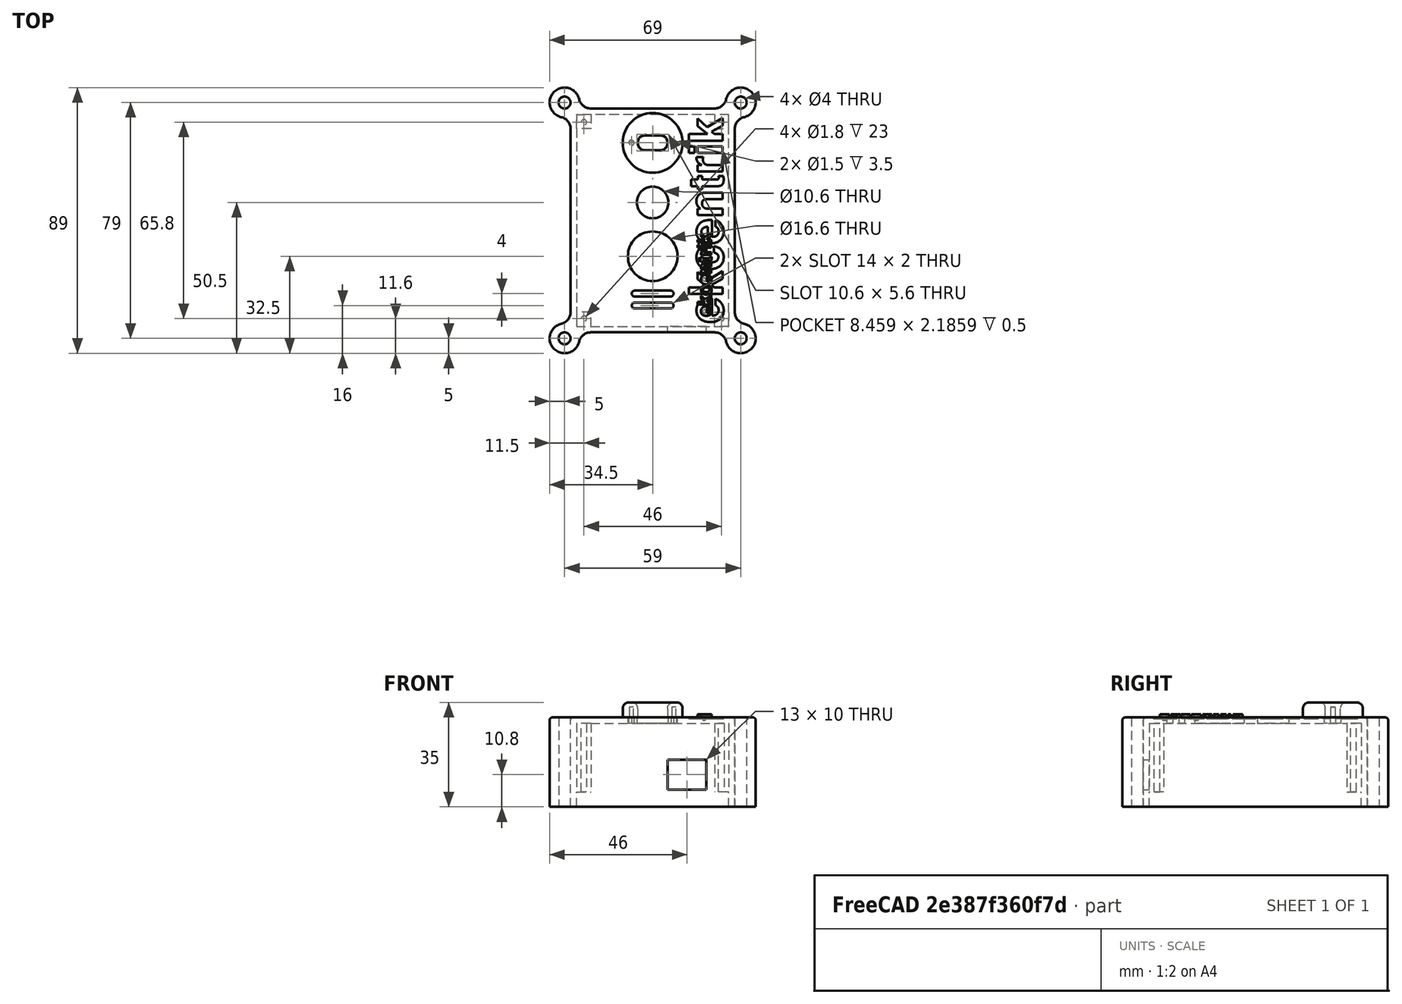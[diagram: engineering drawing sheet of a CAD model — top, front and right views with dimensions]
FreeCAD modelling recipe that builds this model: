
FCSTD DOCUMENT  (FreeCAD 0.18R16110 (Git))
Label: Boitier_V2
License: All rights reserved
LicenseURL: http://en.wikipedia.org/wiki/All_rights_reserved
objects: Sketcher::SketchObject×13, Part::Extrusion×13, Part::Feature×12, PartDesign::Pocket×7, PartDesign::Pad×6, PartDesign::Fillet×4, PartDesign::Body×2, Part::Part2DObjectPython×2, PartDesign::ShapeBinder×1, Mesh::Feature×1, Part::Compound×1, Part::Cut×1
note: 75 computed .brp shape members not serialized (recipe doc carries the construction recipe); baked Part::Feature solids carry a one-line shape summary decoded from their .brp

FEATURE [Sketcher::SketchObject] Sketch
  MapMode = 5
  Support = -> [XY_Plane]
  sketch-geometry (12):
    g0: ArcOfCircle CenterX=-29.5 CenterY=39.5 CenterZ=0 NormalX=0 NormalY=0 NormalZ=1 AngleXU=0 Radius=5 StartAngle=5.87167 EndAngle=11.4071
    g1: ArcOfCircle CenterX=29.5 CenterY=39.5 CenterZ=0 NormalX=0 NormalY=0 NormalZ=1 AngleXU=0 Radius=5 StartAngle=4.30087 EndAngle=9.83629
    g2: ArcOfCircle CenterX=-29.5 CenterY=-39.5 CenterZ=0 NormalX=0 NormalY=0 NormalZ=1 AngleXU=0 Radius=5 StartAngle=1.15928 EndAngle=6.6947
    g3: ArcOfCircle CenterX=29.5 CenterY=-39.5 CenterZ=0 NormalX=0 NormalY=0 NormalZ=1 AngleXU=0 Radius=5 StartAngle=2.73008 EndAngle=8.2655
    g4: LineSegment StartX=27.5 StartY=34.9174 StartZ=0 EndX=27.5 EndY=-34.9174 EndZ=0
    g5: LineSegment StartX=-27.5 StartY=34.9174 StartZ=0 EndX=-27.5 EndY=-34.9174 EndZ=0
    g6: LineSegment StartX=-24.9174 StartY=-37.5 StartZ=0 EndX=24.9174 EndY=-37.5 EndZ=0
    g7: LineSegment StartX=-24.9174 StartY=37.5 StartZ=0 EndX=24.9174 EndY=37.5 EndZ=0
    g8: Circle CenterX=-29.5 CenterY=39.5 CenterZ=0 NormalX=0 NormalY=0 NormalZ=1 AngleXU=0 Radius=2
    g9: Circle CenterX=29.5 CenterY=39.5 CenterZ=0 NormalX=0 NormalY=0 NormalZ=1 AngleXU=0 Radius=2
    g10: Circle CenterX=-29.5 CenterY=-39.5 CenterZ=0 NormalX=0 NormalY=0 NormalZ=1 AngleXU=0 Radius=2
    g11: Circle CenterX=29.5 CenterY=-39.5 CenterZ=0 NormalX=0 NormalY=0 NormalZ=1 AngleXU=0 Radius=2
  constraints (31):
    c: Coincident(g4,g1)
    c: Coincident(g4,g3)
    c: Vertical(g4)
    c: Coincident(g5,g0)
    c: Coincident(g5,g2)
    c: Vertical(g5)
    c: Coincident(g6,g2)
    c: Coincident(g6,g3)
    c: Horizontal(g6)
    c: Coincident(g7,g0)
    c: Horizontal(g7)
    c: Symmetric(g0,g2,g-1)
    c: Symmetric(g1,g3,g-1)
    c: Symmetric(g1,g0,g-2)
    c: Radius(g0) = 5
    c: Equal(g0,g3)
    c: Symmetric(g0,g1,g-2)
    c: Symmetric(g0,g2,g-1)
    c: DistanceX(g-2,g0) = -27.5
    c: DistanceY(g-1,g0) = 37.5
    c: Coincident(g1,g7)
    c: Distance(g0,g5) = 2
    c: Distance(g0,g7) = 2
    c: Coincident(g8,g0)
    c: Coincident(g9,g1)
    c: Coincident(g10,g2)
    c: Coincident(g11,g3)
    c: Radius(g11) = 2
    c: Equal(g11,g10)
    c: Equal(g11,g8)
    c: Equal(g11,g9)
FEATURE [PartDesign::Pad] Pad  label="Envelope externe"
  Length = 30
  Length2 = 100
  Profile = -> Sketch
  Type = 0
FEATURE [Sketcher::SketchObject] Sketch001
  MapMode = 5
  Placement = pos=(0,0,0) rot=(1,0,0;3.14159rad)
  Support = -> [Pad]
  sketch-geometry (4):
    g0: LineSegment StartX=-25.5 StartY=35.5 StartZ=0 EndX=25.5 EndY=35.5 EndZ=0
    g1: LineSegment StartX=25.5 StartY=35.5 StartZ=0 EndX=25.5 EndY=-35.5 EndZ=0
    g2: LineSegment StartX=25.5 StartY=-35.5 StartZ=0 EndX=-25.5 EndY=-35.5 EndZ=0
    g3: LineSegment StartX=-25.5 StartY=-35.5 StartZ=0 EndX=-25.5 EndY=35.5 EndZ=0
  constraints (10):
    c: Coincident(g0,g1)
    c: Coincident(g1,g2)
    c: Coincident(g2,g3)
    c: Coincident(g3,g0)
    c: Horizontal(g2)
    c: Vertical(g1)
    c: Symmetric(g0,g2,g-1)
    c: Symmetric(g0,g0,g-2)
    c: DistanceX(g0,g0) = 51
    c: DistanceY(g1,g1) = 71
FEATURE [PartDesign::Pocket] Pocket  label="Cavite interne"
  BaseFeature = -> Pad
  Length = 28
  Length2 = 100
  Profile = -> Sketch001
  Type = 0
FEATURE [Sketcher::SketchObject] Sketch002
  ExternalGeometry = -> [Pocket]
  MapMode = 5
  Placement = pos=(0,0,28) rot=(1,0,0;3.14159rad)
  Support = -> [Pocket]
  sketch-geometry (5):
    g0: Circle CenterX=-23 CenterY=32.9 CenterZ=0 NormalX=0 NormalY=0 NormalZ=1 AngleXU=0 Radius=0.9
    g1: LineSegment StartX=-25.5 StartY=35.5 StartZ=0 EndX=-20.7 EndY=35.5 EndZ=0
    g2: LineSegment StartX=-20.7 StartY=35.5 StartZ=0 EndX=-20.7 EndY=30.7 EndZ=0
    g3: LineSegment StartX=-20.7 StartY=30.7 StartZ=0 EndX=-25.5 EndY=30.7 EndZ=0
    g4: LineSegment StartX=-25.5 StartY=30.7 StartZ=0 EndX=-25.5 EndY=35.5 EndZ=0
  constraints (14):
    c: Coincident(g1,g2)
    c: Coincident(g2,g3)
    c: Coincident(g3,g4)
    c: Coincident(g4,g1)
    c: Horizontal(g1)
    c: Horizontal(g3)
    c: Vertical(g2)
    c: Vertical(g4)
    c: Coincident(g1,g-4)
    c: Radius(g0) = 0.9
    c: Distance(g3) = 4.8
    c: DistanceX(g-2,g0) = -23
    c: DistanceY(g-1,g0) = 32.9
    c: Distance(g2) = 4.8
FEATURE [PartDesign::Pad] Pad001  label="Pilier PCB 1"
  BaseFeature = -> Pocket
  Length = 23
  Length2 = 100
  Profile = -> Sketch002
  Type = 0
FEATURE [Sketcher::SketchObject] Sketch003
  ExternalGeometry = -> [Pad001]
  MapMode = 5
  Placement = pos=(0,0,28) rot=(1,0,0;3.14159rad)
  Support = -> [Pad001]
  sketch-geometry (5):
    g0: LineSegment StartX=25.5 StartY=35.5 StartZ=0 EndX=20.7 EndY=35.5 EndZ=0
    g1: LineSegment StartX=20.7 StartY=35.5 StartZ=0 EndX=20.7 EndY=30.7 EndZ=0
    g2: LineSegment StartX=20.7 StartY=30.7 StartZ=0 EndX=25.5 EndY=30.7 EndZ=0
    g3: LineSegment StartX=25.5 StartY=30.7 StartZ=0 EndX=25.5 EndY=35.5 EndZ=0
    g4: Circle CenterX=23 CenterY=32.9 CenterZ=0 NormalX=0 NormalY=0 NormalZ=1 AngleXU=0 Radius=0.9
  constraints (14):
    c: Coincident(g0,g1)
    c: Coincident(g1,g2)
    c: Coincident(g2,g3)
    c: Coincident(g3,g0)
    c: Horizontal(g0)
    c: Horizontal(g2)
    c: Vertical(g1)
    c: Vertical(g3)
    c: Coincident(g0,g-4)
    c: DistanceY(g1,g1) = 4.8
    c: DistanceX(g2,g2) = 4.8
    c: Radius(g4) = 0.9
    c: DistanceX(g-2,g4) = 23
    c: DistanceY(g-1,g4) = 32.9
FEATURE [PartDesign::Pad] Pad002  label="Pilier PCB 2"
  BaseFeature = -> Pad001
  Length = 23
  Length2 = 100
  Profile = -> Sketch003
  Type = 0
FEATURE [Sketcher::SketchObject] Sketch004
  ExternalGeometry = -> [Pad002]
  MapMode = 5
  Placement = pos=(0,0,28) rot=(1,0,0;3.14159rad)
  Support = -> [Pad002]
  sketch-geometry (5):
    g0: LineSegment StartX=25.5 StartY=-35.5 StartZ=0 EndX=20.7 EndY=-35.5 EndZ=0
    g1: LineSegment StartX=20.7 StartY=-35.5 StartZ=0 EndX=20.7 EndY=-30.7 EndZ=0
    g2: LineSegment StartX=20.7 StartY=-30.7 StartZ=0 EndX=25.5 EndY=-30.7 EndZ=0
    g3: LineSegment StartX=25.5 StartY=-30.7 StartZ=0 EndX=25.5 EndY=-35.5 EndZ=0
    g4: Circle CenterX=23 CenterY=-32.9 CenterZ=0 NormalX=0 NormalY=0 NormalZ=1 AngleXU=0 Radius=0.9
  constraints (14):
    c: Coincident(g0,g1)
    c: Coincident(g1,g2)
    c: Coincident(g2,g3)
    c: Coincident(g3,g0)
    c: Horizontal(g0)
    c: Horizontal(g2)
    c: Vertical(g1)
    c: Vertical(g3)
    c: Coincident(g0,g-4)
    c: DistanceX(g2,g2) = 4.8
    c: DistanceY(g1,g1) = 4.8
    c: Radius(g4) = 0.9
    c: DistanceX(g-2,g4) = 23
    c: DistanceY(g-1,g4) = -32.9
FEATURE [PartDesign::Pad] Pad003  label="Pilier PCB 3"
  BaseFeature = -> Pad002
  Length = 23
  Length2 = 100
  Profile = -> Sketch004
  Type = 0
FEATURE [Sketcher::SketchObject] Sketch005
  ExternalGeometry = -> [Pad003]
  MapMode = 5
  Placement = pos=(0,0,28) rot=(1,0,0;3.14159rad)
  Support = -> [Pad003]
  sketch-geometry (5):
    g0: LineSegment StartX=-25.5 StartY=-35.5 StartZ=0 EndX=-20.7 EndY=-35.5 EndZ=0
    g1: LineSegment StartX=-20.7 StartY=-35.5 StartZ=0 EndX=-20.7 EndY=-30.7 EndZ=0
    g2: LineSegment StartX=-20.7 StartY=-30.7 StartZ=0 EndX=-25.5 EndY=-30.7 EndZ=0
    g3: LineSegment StartX=-25.5 StartY=-30.7 StartZ=0 EndX=-25.5 EndY=-35.5 EndZ=0
    g4: Circle CenterX=-23 CenterY=-32.9 CenterZ=0 NormalX=0 NormalY=0 NormalZ=1 AngleXU=0 Radius=0.9
  constraints (14):
    c: Coincident(g0,g1)
    c: Coincident(g1,g2)
    c: Coincident(g2,g3)
    c: Coincident(g3,g0)
    c: Horizontal(g0)
    c: Horizontal(g2)
    c: Vertical(g1)
    c: Vertical(g3)
    c: Coincident(g0,g-4)
    c: DistanceX(g2,g2) = 4.8
    c: DistanceY(g1,g1) = 4.8
    c: Radius(g4) = 0.9
    c: DistanceX(g-2,g4) = -23
    c: DistanceY(g-1,g4) = -32.9
FEATURE [PartDesign::Pad] Pad004  label="Pilier PCB 4"
  BaseFeature = -> Pad003
  Length = 23
  Length2 = 100
  Profile = -> Sketch005
  Type = 0
FEATURE [Sketcher::SketchObject] Sketch006
  ExternalGeometry = -> [Pad004]
  MapMode = 5
  Placement = pos=(0,0,28) rot=(1,0,0;3.14159rad)
  Support = -> [Pad004]
  sketch-geometry (1):
    g0: Circle CenterX=0 CenterY=-6 CenterZ=0 NormalX=0 NormalY=0 NormalZ=1 AngleXU=0 Radius=5.3
  constraints (3):
    c: PointOnObject(g0,g-2)
    c: Distance(g0,g-3) = 41.5
    c: Radius(g0) = 5.3
FEATURE [PartDesign::Pocket] Pocket001  label="Percage LED"
  BaseFeature = -> Pad004
  Length = 5
  Length2 = 100
  Profile = -> Sketch006
  Type = 0
FEATURE [Sketcher::SketchObject] Sketch007
  MapMode = 5
  Placement = pos=(0,0,28) rot=(1,0,0;3.14159rad)
  Support = -> [Pocket001]
  sketch-geometry (1):
    g0: Circle CenterX=0 CenterY=12 CenterZ=0 NormalX=0 NormalY=0 NormalZ=1 AngleXU=0 Radius=8.3
  constraints (3):
    c: PointOnObject(g0,g-2)
    c: Radius(g0) = 8.3
    c: DistanceY(g-1,g0) = 12
FEATURE [PartDesign::Pocket] Pocket002  label="Percage bouton"
  BaseFeature = -> Pocket001
  Length = 5
  Length2 = 100
  Profile = -> Sketch007
  Type = 0
FEATURE [Sketcher::SketchObject] Sketch008
  ExternalGeometry = -> [Pocket002]
  MapMode = 5
  Placement = pos=(0,0,28) rot=(1,0,0;3.14159rad)
  Support = -> [Pocket002]
  sketch-geometry (8):
    g0: ArcOfCircle CenterX=-6 CenterY=28.5 CenterZ=0 NormalX=0 NormalY=0 NormalZ=1 AngleXU=0 Radius=1 StartAngle=1.5708 EndAngle=4.71239
    g1: ArcOfCircle CenterX=6 CenterY=28.5 CenterZ=0 NormalX=0 NormalY=0 NormalZ=1 AngleXU=0 Radius=1 StartAngle=4.71239 EndAngle=7.85398
    g2: LineSegment StartX=-6 StartY=27.5 StartZ=0 EndX=6 EndY=27.5 EndZ=0
    g3: LineSegment StartX=-6 StartY=29.5 StartZ=0 EndX=6 EndY=29.5 EndZ=0
    g4: ArcOfCircle CenterX=-6 CenterY=24.5 CenterZ=0 NormalX=0 NormalY=0 NormalZ=1 AngleXU=0 Radius=1 StartAngle=1.5708 EndAngle=4.71239
    g5: ArcOfCircle CenterX=6 CenterY=24.5 CenterZ=0 NormalX=0 NormalY=0 NormalZ=1 AngleXU=0 Radius=1 StartAngle=4.71239 EndAngle=7.85398
    g6: LineSegment StartX=-6 StartY=23.5 StartZ=0 EndX=6 EndY=23.5 EndZ=0
    g7: LineSegment StartX=-6 StartY=25.5 StartZ=0 EndX=6 EndY=25.5 EndZ=0
  constraints (18):
    c: Tangent(g0,g3) = 1.5708
    c: Tangent(g0,g2) = -1.5708
    c: Tangent(g2,g1) = -1.5708
    c: Tangent(g3,g1) = 1.5708
    c: Horizontal(g2)
    c: Tangent(g4,g7) = 1.5708
    c: Tangent(g4,g6) = -1.5708
    c: Tangent(g6,g5) = -1.5708
    c: Tangent(g7,g5) = 1.5708
    c: Horizontal(g6)
    c: Symmetric(g0,g1,g-2)
    c: Symmetric(g4,g5,g-2)
    c: Radius(g1) = 1
    c: Radius(g5) = 1
    c: Distance(g1,g7) = 2
    c: Distance(g3) = 12
    c: Distance(g7) = 12
    c: Distance(g1,g-3) = 6
FEATURE [PartDesign::Pocket] Pocket003  label="Percage buzzer"
  BaseFeature = -> Pocket002
  Length = 5
  Length2 = 100
  Profile = -> Sketch008
  Type = 0
FEATURE [Sketcher::SketchObject] Sketch009
  ExternalGeometry = -> [Pocket003]
  MapMode = 5
  Placement = pos=(0,-37.5,0) rot=(1,0,0;1.5708rad)
  Support = -> [Pocket003]
  sketch-geometry (4):
    g0: LineSegment StartX=5 StartY=15.8 StartZ=0 EndX=18 EndY=15.8 EndZ=0
    g1: LineSegment StartX=18 StartY=15.8 StartZ=0 EndX=18 EndY=5.8 EndZ=0
    g2: LineSegment StartX=18 StartY=5.8 StartZ=0 EndX=5 EndY=5.8 EndZ=0
    g3: LineSegment StartX=5 StartY=5.8 StartZ=0 EndX=5 EndY=15.8 EndZ=0
  constraints (12):
    c: Coincident(g0,g1)
    c: Coincident(g1,g2)
    c: Coincident(g2,g3)
    c: Coincident(g3,g0)
    c: Horizontal(g0)
    c: Horizontal(g2)
    c: Vertical(g1)
    c: Vertical(g3)
    c: DistanceX(g0,g0) = 13
    c: DistanceY(g1,g1) = 10
    c: DistanceX(g-2,g2) = 5
    c: Distance(g1,g-3) = 0.8
FEATURE [PartDesign::Pocket] Pocket004  label="Percage USB"
  BaseFeature = -> Pocket003
  Length = 5
  Length2 = 100
  Profile = -> Sketch009
  Type = 0
FEATURE [Sketcher::SketchObject] Sketch010
  ExternalGeometry = -> [Pocket004]
  MapMode = 5
  Placement = pos=(0,0,28) rot=(1,0,0;3.14159rad)
  Support = -> [Pocket004]
  sketch-geometry (6):
    g0: ArcOfCircle CenterX=-2.5 CenterY=-26 CenterZ=0 NormalX=0 NormalY=0 NormalZ=1 AngleXU=0 Radius=2.8 StartAngle=1.5708 EndAngle=4.71239
    g1: ArcOfCircle CenterX=2.5 CenterY=-26 CenterZ=0 NormalX=0 NormalY=0 NormalZ=1 AngleXU=0 Radius=2.8 StartAngle=4.71239 EndAngle=7.85398
    g2: LineSegment StartX=-2.5 StartY=-28.8 StartZ=0 EndX=2.5 EndY=-28.8 EndZ=0
    g3: LineSegment StartX=-2.5 StartY=-23.2 StartZ=0 EndX=2.5 EndY=-23.2 EndZ=0
    g4: Circle CenterX=-7.115 CenterY=-26 CenterZ=0 NormalX=0 NormalY=0 NormalZ=1 AngleXU=0 Radius=0.9
    g5: Circle CenterX=7.115 CenterY=-26 CenterZ=0 NormalX=0 NormalY=0 NormalZ=1 AngleXU=0 Radius=0.9
  constraints (14):
    c: Tangent(g0,g3) = 1.5708
    c: Tangent(g0,g2) = -1.5708
    c: Tangent(g2,g1) = -1.5708
    c: Tangent(g3,g1) = 1.5708
    c: Horizontal(g2)
    c: Radius(g1) = 2.8
    c: DistanceX(g3,g3) = 5
    c: Symmetric(g0,g1,g-2)
    c: Symmetric(g5,g4,g-2)
    c: DistanceX(g-2,g4) = -7.115
    c: Radius(g4) = 0.9
    c: Equal(g4,g5)
    c: DistanceY(g-1,g5) = -26
    c: DistanceY(g-1,g1) = -26
FEATURE [PartDesign::Pocket] Pocket005  label="Percage TOF10120"
  BaseFeature = -> Pocket004
  Length = 5
  Length2 = 100
  Profile = -> Sketch010
  Type = 0
FEATURE [PartDesign::ShapeBinder] CopyPocket005
  TraceSupport = false
FEATURE [Sketcher::SketchObject] Sketch011
  MapMode = 5
  Placement = pos=(0,0,30) rot=(0,0,1;0rad)
  Support = -> [CopyPocket005]
  sketch-geometry (5):
    g0: ArcOfCircle CenterX=-2.5 CenterY=26 CenterZ=0 NormalX=0 NormalY=0 NormalZ=1 AngleXU=0 Radius=2.5 StartAngle=1.5708 EndAngle=4.71239
    g1: ArcOfCircle CenterX=2.5 CenterY=26 CenterZ=0 NormalX=0 NormalY=0 NormalZ=1 AngleXU=0 Radius=2.5 StartAngle=4.71239 EndAngle=7.85398
    g2: LineSegment StartX=-2.5 StartY=23.5 StartZ=0 EndX=2.5 EndY=23.5 EndZ=0
    g3: LineSegment StartX=-2.5 StartY=28.5 StartZ=0 EndX=2.5 EndY=28.5 EndZ=0
    g4: Circle CenterX=0.000374 CenterY=26 CenterZ=0 NormalX=0 NormalY=0 NormalZ=1 AngleXU=0 Radius=10
  constraints (11):
    c: Tangent(g0,g3) = 1.5708
    c: Tangent(g0,g2) = -1.5708
    c: Tangent(g2,g1) = -1.5708
    c: Tangent(g3,g1) = 1.5708
    c: Horizontal(g2)
    c: Radius(g1) = 2.5
    c: DistanceX(g3,g3) = 5
    c: Symmetric(g1,g0,g-2)
    c: DistanceY(g-1,g1) = 26
    c: DistanceY(g-1,g4) = 26
    c: Radius(g4) = 10
FEATURE [PartDesign::Pad] Pad005  label="Forme generale"
  Length = 5
  Length2 = 100
  Profile = -> Sketch011
  Type = 0
FEATURE [PartDesign::Fillet] Fillet
  Base = -> Pad005 [Edge15]
  BaseFeature = -> Pad005
  Radius = 2
FEATURE [PartDesign::Fillet] Fillet001
  Base = -> Fillet [Edge22]
  BaseFeature = -> Fillet
  Radius = 2
FEATURE [Sketcher::SketchObject] Sketch012
  MapMode = 5
  Placement = pos=(0,0,30) rot=(1,0,0;3.14159rad)
  Support = -> [Fillet001]
  sketch-geometry (2):
    g0: Circle CenterX=-7.115 CenterY=-26 CenterZ=0 NormalX=0 NormalY=0 NormalZ=1 AngleXU=0 Radius=0.75
    g1: Circle CenterX=7.115 CenterY=-26 CenterZ=0 NormalX=0 NormalY=0 NormalZ=1 AngleXU=0 Radius=0.75
  constraints (5):
    c: Symmetric(g0,g1,g-2)
    c: Radius(g0) = 0.75
    c: Equal(g0,g1)
    c: DistanceY(g-1,g0) = -26
    c: DistanceX(g-2,g0) = -7.115
FEATURE [PartDesign::Pocket] Pocket006
  BaseFeature = -> Fillet001
  Length = 3.5
  Length2 = 100
  Profile = -> Sketch012
  Type = 0
FEATURE [PartDesign::Body] Body001  label="Protecteur TOF"
  Group = -> [CopyPocket005,Sketch011,Pad005,Fillet,Fillet001,Sketch012,Pocket006]
  Origin = -> Origin001
  Tip = -> Pocket006
FEATURE [Mesh::Feature] Mesh  label="Protecteur TOF (Meshed)"
FEATURE [PartDesign::Fillet] Fillet002
  Base = -> Pocket005 [Edge2,Edge1,Edge49,Edge5,Edge50,Edge8,Edge51,Edge52]
  BaseFeature = -> Pocket005
  Radius = 4
FEATURE [PartDesign::Fillet] Fillet003
  Base = -> Fillet002 [Edge40]
  BaseFeature = -> Fillet002
  Radius = 1
FEATURE [PartDesign::Body] Body  label="Boitier PCB"
  Group = -> [Sketch,Pad,Sketch001,Pocket,Sketch002,Pad001,Sketch003,Pad002,Sketch004,Pad003,Sketch005,Pad004,Sketch006,Pocket001,Sketch007,Pocket002,Sketch008,Pocket003,Sketch009,Pocket004,Sketch010,Pocket005,Fillet002,Fillet003]
  Origin = -> Origin
  Tip = -> Fillet003
FEATURE [Part::Feature] Face
  shape: bbox 3.105 x 4.629 x 2e-07 mm, 1 faces, 0 solids (baked)
FEATURE [Part::Feature] Face001
  shape: bbox 0.889 x 0.7938 x 2e-07 mm, 1 faces, 0 solids (baked)
FEATURE [Part::Feature] Face002
  shape: bbox 0.889 x 3.429 x 2e-07 mm, 1 faces, 0 solids (baked)
FEATURE [Part::Feature] Face003
  shape: bbox 1.949 x 3.486 x 2e-07 mm, 1 faces, 0 solids (baked)
FEATURE [Part::Feature] Face004
  shape: bbox 1.822 x 4.426 x 2e-07 mm, 1 faces, 0 solids (baked)
FEATURE [Part::Feature] Face005
  shape: bbox 3.067 x 3.486 x 2e-07 mm, 1 faces, 0 solids (baked)
FEATURE [Part::Feature] Face006
  shape: bbox 1.365 x 0.7811 x 2e-07 mm, 1 faces, 0 solids (baked)
FEATURE [Part::Feature] Face007
  shape: bbox 3.194 x 3.632 x 2e-07 mm, 1 faces, 0 solids (baked)
FEATURE [Part::Feature] Face008
  shape: bbox 3.099 x 3.632 x 2e-07 mm, 1 faces, 0 solids (baked)
FEATURE [Part::Feature] Face009
  shape: bbox 3.105 x 4.629 x 2e-07 mm, 1 faces, 0 solids (baked)
FEATURE [Part::Feature] Face010
  shape: bbox 1.365 x 0.7811 x 2e-07 mm, 1 faces, 0 solids (baked)
FEATURE [Part::Feature] Face011
  shape: bbox 3.194 x 3.632 x 2e-07 mm, 1 faces, 0 solids (baked)
FEATURE [Part::Extrusion] Extrude
  Base = -> Face
  Dir = (0,0,1)
  DirMode = 2
  FaceMakerClass = Part::FaceMakerBullseye
  LengthFwd = 1
  LengthRev = 0
  Solid = false
  Symmetric = false
FEATURE [Part::Extrusion] Extrude001
  Base = -> Face001
  Dir = (0,0,1)
  DirMode = 2
  FaceMakerClass = Part::FaceMakerBullseye
  LengthFwd = 1
  LengthRev = 0
  Solid = false
  Symmetric = false
FEATURE [Part::Extrusion] Extrude002
  Base = -> Face002
  Dir = (0,0,1)
  DirMode = 2
  FaceMakerClass = Part::FaceMakerBullseye
  LengthFwd = 1
  LengthRev = 0
  Solid = false
  Symmetric = false
FEATURE [Part::Extrusion] Extrude003
  Base = -> Face003
  Dir = (0,0,1)
  DirMode = 2
  FaceMakerClass = Part::FaceMakerBullseye
  LengthFwd = 1
  LengthRev = 0
  Solid = false
  Symmetric = false
FEATURE [Part::Extrusion] Extrude004
  Base = -> Face004
  Dir = (0,0,1)
  DirMode = 2
  FaceMakerClass = Part::FaceMakerBullseye
  LengthFwd = 1
  LengthRev = 0
  Solid = false
  Symmetric = false
FEATURE [Part::Extrusion] Extrude005
  Base = -> Face005
  Dir = (0,0,1)
  DirMode = 2
  FaceMakerClass = Part::FaceMakerBullseye
  LengthFwd = 1
  LengthRev = 0
  Solid = false
  Symmetric = false
FEATURE [Part::Extrusion] Extrude006
  Base = -> Face006
  Dir = (0,0,-1)
  DirMode = 2
  FaceMakerClass = Part::FaceMakerBullseye
  LengthFwd = 1
  LengthRev = 0
  Solid = false
  Symmetric = false
FEATURE [Part::Extrusion] Extrude007
  Base = -> Face007
  Dir = (0,0,1)
  DirMode = 2
  FaceMakerClass = Part::FaceMakerBullseye
  LengthFwd = 1
  LengthRev = 0
  Solid = false
  Symmetric = false
FEATURE [Part::Extrusion] Extrude008
  Base = -> Face008
  Dir = (0,0,1)
  DirMode = 2
  FaceMakerClass = Part::FaceMakerBullseye
  LengthFwd = 1
  LengthRev = 0
  Solid = false
  Symmetric = false
FEATURE [Part::Extrusion] Extrude009
  Base = -> Face009
  Dir = (0,0,1)
  DirMode = 2
  FaceMakerClass = Part::FaceMakerBullseye
  LengthFwd = 1
  LengthRev = 0
  Solid = false
  Symmetric = false
FEATURE [Part::Extrusion] Extrude010
  Base = -> Face010
  Dir = (0,0,-1)
  DirMode = 2
  FaceMakerClass = Part::FaceMakerBullseye
  LengthFwd = 1
  LengthRev = 0
  Solid = false
  Symmetric = false
FEATURE [Part::Extrusion] Extrude011
  Base = -> Face011
  Dir = (0,0,1)
  DirMode = 2
  FaceMakerClass = Part::FaceMakerBullseye
  LengthFwd = 1
  LengthRev = 0
  Solid = false
  Symmetric = false
FEATURE [Part::Compound] Compound  label="ekcentrik_texte"
  Links = -> [Extrude,Extrude008,Extrude002,Extrude003,Extrude005,Extrude009,Extrude006,Extrude001,Extrude007,Extrude004,Extrude010,Extrude011]
  Placement = pos=(15,-32,30) rot=(0,0,1;1.5708rad)
FEATURE [Part::Part2DObjectPython] ShapeString002  # Draft 2D object (typed FeaturePython)
  FontFile = <path>
  Placement = pos=(-182.16,-26.36,0) rot=(0,0,1;0rad)
  Size = 8
  String = ekcentrik
  Tracking = 0
FEATURE [Part::Part2DObjectPython] ShapeString  # Draft 2D object (typed FeaturePython)
  FontFile = <path>
  Placement = pos=(15.12,-10.95,0) rot=(0,0,1;0rad)
  Size = 7
  String = ekcentrik
  Tracking = 0
FEATURE [Part::Extrusion] Extrude012
  Base = -> ShapeString
  Dir = (0,0,1)
  DirMode = 2
  FaceMakerClass = Part::FaceMakerBullseye
  LengthFwd = 0.5
  LengthRev = 0
  Placement = pos=(12.5,-49.5,29.5) rot=(0,0,1;1.5708rad)
  Solid = false
  Symmetric = false
FEATURE [Part::Cut] Cut
  Base = -> Body
  Tool = -> Extrude012
note: 2 file-system paths scrubbed to <path> (originals preserved in the JSON sidecar)
